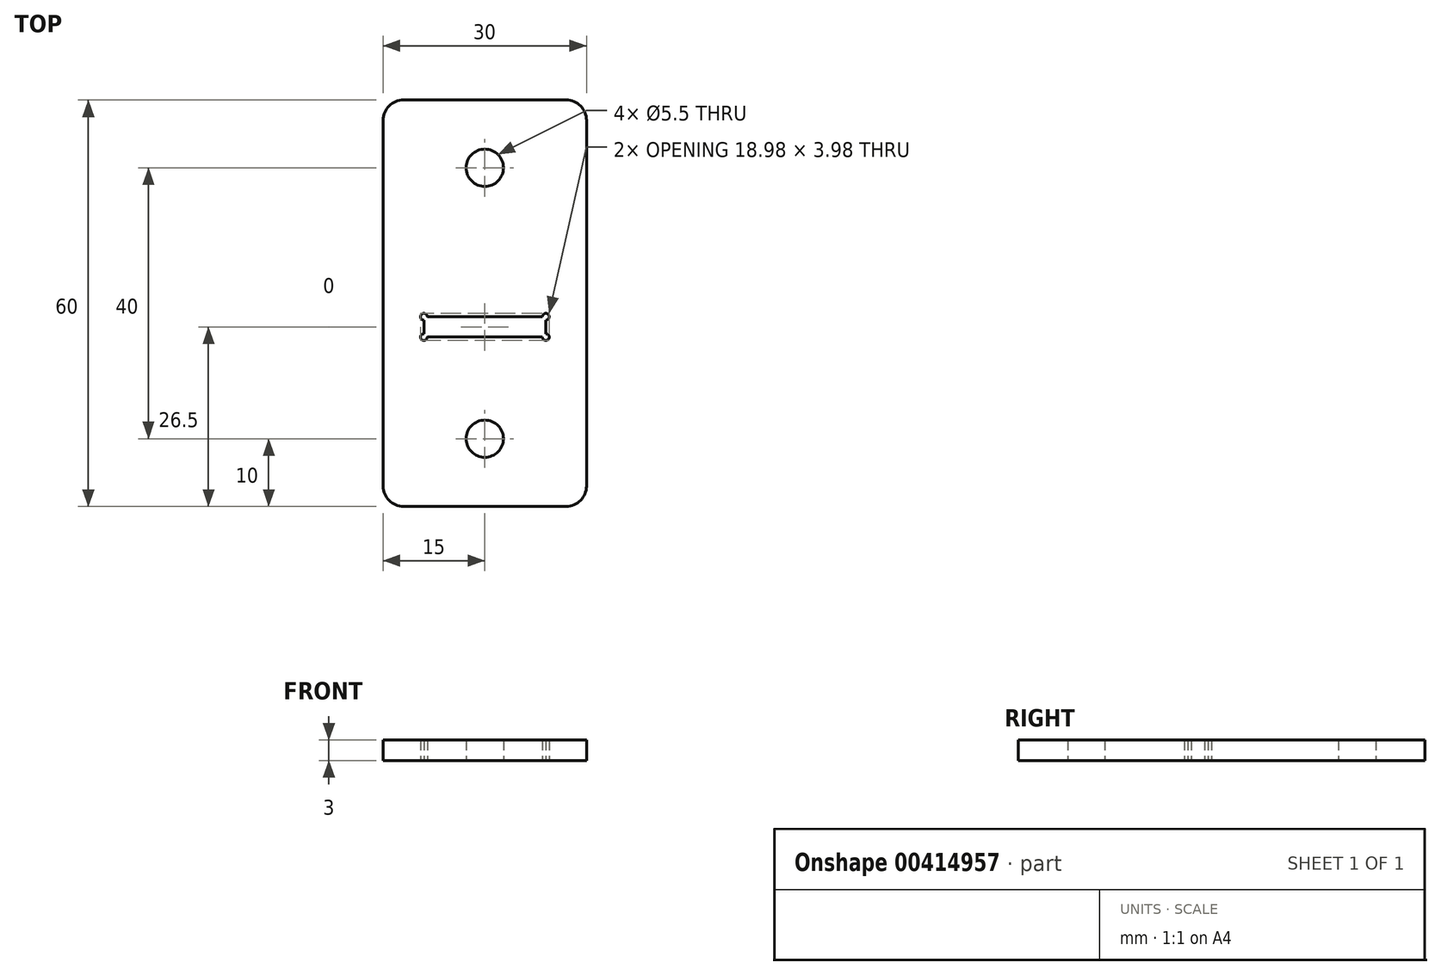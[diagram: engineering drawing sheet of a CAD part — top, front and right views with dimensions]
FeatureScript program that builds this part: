
annotation { "Feature Type Name" : "Feature", "Feature Type Description" : "" }
export const myFeature = defineFeature(function(context is Context, id is Id, definition is map)
    precondition{}
    {
        {
            var Q0;
            Q0=qCreatedBy(makeId("Top.planeOp"),FACE);
            var sketch = newSketch(context, id + "F0", { "sketchPlane" : qUnion([Q0])});
            skLineSegment(sketch, "E0.bottom", {"start": v(3, 0) * mm, "end": v(27, 0) * mm});
            skLineSegment(sketch, "E0.top", {"start": v(3, 60) * mm, "end": v(27, 60) * mm});
            skLineSegment(sketch, "E0.left", {"start": v(0, 3) * mm, "end": v(0, 57) * mm});
            skLineSegment(sketch, "E0.right", {"start": v(30, 3) * mm, "end": v(30, 57) * mm});
            skCircle(sketch, "E1", {"center": v(15, 10) * mm, "radius": 2.75 * mm});
            skPoint(sketch, "E1.centerSnap0", {"position": v(15, 0) * mm});
            skCircle(sketch, "E2", {"center": v(15, 50) * mm, "radius": 2.75 * mm});
            skLineSegment(sketch, "E3.bottom", {"start": v(6, 28) * mm, "end": v(24, 28) * mm});
            skLineSegment(sketch, "E3.top", {"start": v(6, 25) * mm, "end": v(24, 25) * mm});
            skLineSegment(sketch, "E3.left", {"start": v(6, 28) * mm, "end": v(6, 25) * mm});
            skLineSegment(sketch, "E3.right", {"start": v(24, 28) * mm, "end": v(24, 25) * mm});
            skCircle(sketch, "E4", {"center": v(6, 28) * mm, "radius": 0.5 * mm});
            skCircle(sketch, "E5", {"center": v(6, 25) * mm, "radius": 0.5 * mm});
            skCircle(sketch, "E6", {"center": v(24, 28) * mm, "radius": 0.5 * mm});
            skCircle(sketch, "E7", {"center": v(24, 25) * mm, "radius": 0.5 * mm});
            skPoint(sketch, "E8.visualSharp", {"position": v(0, 60) * mm});
            skArc(sketch, "E8.filletArc", {"start": v(3, 60) * mm, "mid": v(0.88, 59.12) * mm, "end": v(0, 57) * mm});
            skPoint(sketch, "E9.visualSharp", {"position": v(30, 60) * mm});
            skArc(sketch, "E9.filletArc", {"start": v(30, 57) * mm, "mid": v(29.12, 59.12) * mm, "end": v(27, 60) * mm});
            skPoint(sketch, "E10.visualSharp", {"position": v(30, 0) * mm});
            skArc(sketch, "E10.filletArc", {"start": v(27, 0) * mm, "mid": v(29.12, 0.88) * mm, "end": v(30, 3) * mm});
            skPoint(sketch, "E11.visualSharp", {"position": v(0, 0) * mm});
            skArc(sketch, "E11.filletArc", {"start": v(0, 3) * mm, "mid": v(0.88, 0.88) * mm, "end": v(3, 0) * mm});
            skSolve(sketch);
        }
        {
            var Q0;
            Q0=makeQuery(id+"F0.imprint","IMPRINT",FACE,{"disambiguationData":[TD([[makeQuery(id+"F0.imprint","IMPRINT",EDGE,{"derivedFrom":sQuery(id+"F0.wireOp",EDGE,"E0.bottom")}),1.0]])]});
            extrude(context, id + "F1", {"entities" : qUnion([Q0]), "depth" : 3 * mm});
        }
    });
